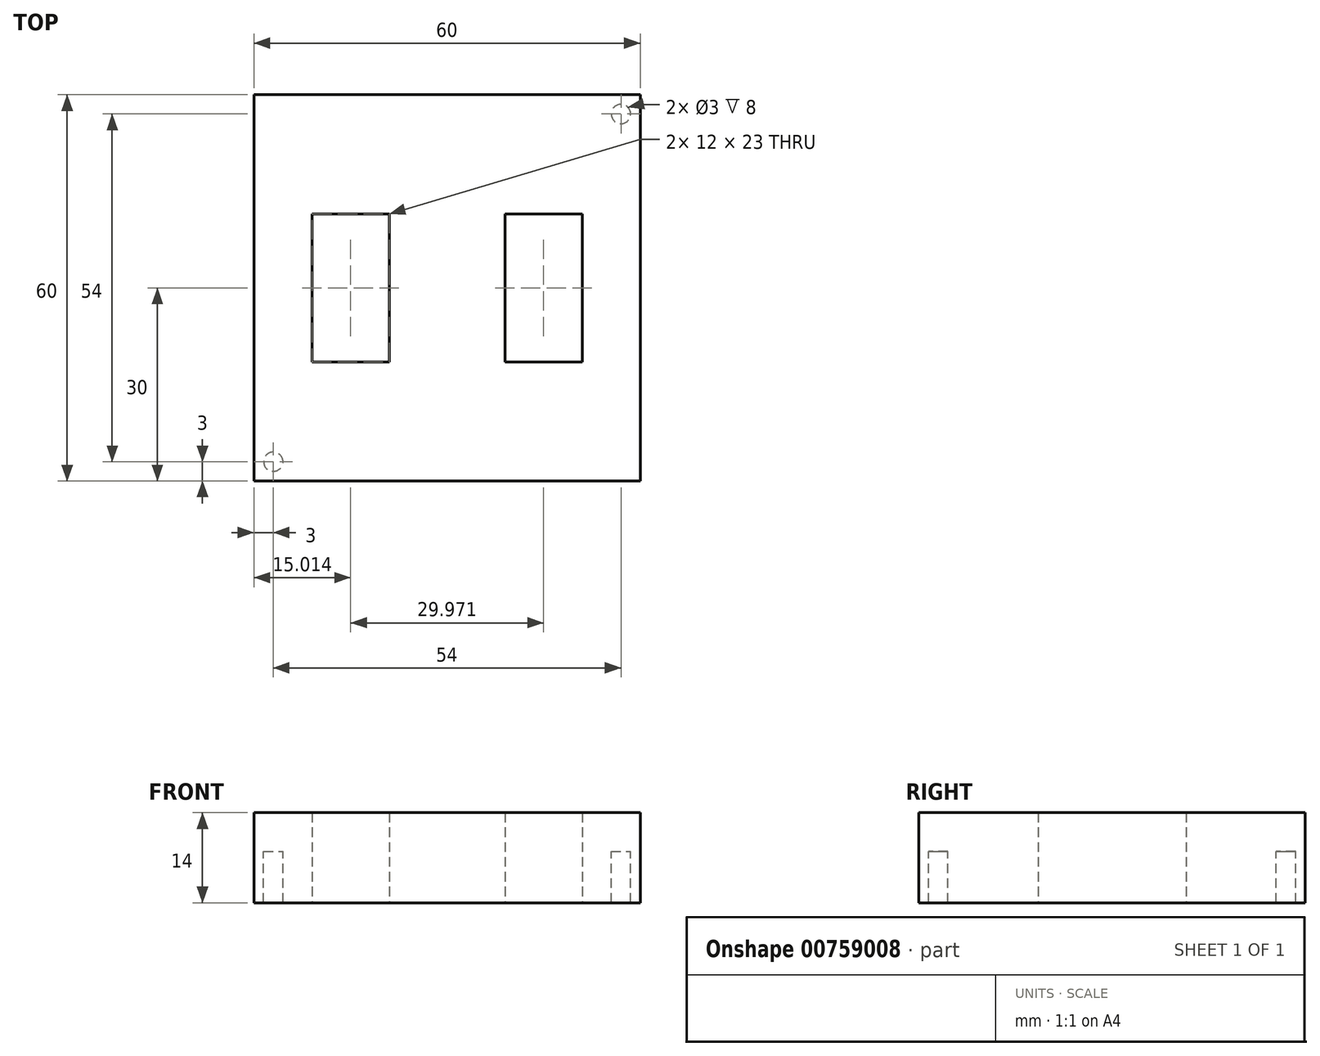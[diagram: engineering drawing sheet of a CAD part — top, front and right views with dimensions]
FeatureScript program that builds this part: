
annotation { "Feature Type Name" : "Feature", "Feature Type Description" : "" }
export const myFeature = defineFeature(function(context is Context, id is Id, definition is map)
    precondition{}
    {
        {
            var Q0;
            Q0=qCreatedBy(makeId("Top.planeOp"),FACE);
            var sketch = newSketch(context, id + "F0", { "sketchPlane" : qUnion([Q0])});
            skLineSegment(sketch, "E0.bottom", {"start": v(-30, 30) * mm, "end": v(30, 30) * mm});
            skLineSegment(sketch, "E0.top", {"start": v(-30, -30) * mm, "end": v(30, -30) * mm});
            skLineSegment(sketch, "E0.left", {"start": v(-30, 30) * mm, "end": v(-30, -30) * mm});
            skLineSegment(sketch, "E0.right", {"start": v(30, 30) * mm, "end": v(30, -30) * mm});
            skPoint(sketch, "E0.middle", {"position": v(0, 0) * mm});
            skLineSegment(sketch, "E1.bottom", {"start": v(8.99, 11.5) * mm, "end": v(20.99, 11.5) * mm});
            skLineSegment(sketch, "E1.top", {"start": v(8.99, -11.5) * mm, "end": v(20.99, -11.5) * mm});
            skLineSegment(sketch, "E1.left", {"start": v(8.99, 11.5) * mm, "end": v(8.99, -11.5) * mm});
            skLineSegment(sketch, "E1.right", {"start": v(20.99, 11.5) * mm, "end": v(20.99, -11.5) * mm});
            skPoint(sketch, "E1.middle", {"position": v(14.99, 0) * mm});
            skLineSegment(sketch, "E2.MirrorCS", {"start": v(-8.99, 11.5) * mm, "end": v(-20.99, 11.5) * mm});
            skLineSegment(sketch, "E3.MirrorCS", {"start": v(-8.99, 11.5) * mm, "end": v(-8.99, -11.5) * mm});
            skLineSegment(sketch, "E4.MirrorCS", {"start": v(-8.99, -11.5) * mm, "end": v(-20.99, -11.5) * mm});
            skLineSegment(sketch, "E5.MirrorCS", {"start": v(-20.99, 11.5) * mm, "end": v(-20.99, -11.5) * mm});
            skSolve(sketch);
        }
        {
            var Q0;
            Q0=makeQuery(id+"F0.imprint","IMPRINT",FACE,{"disambiguationData":[TD([[makeQuery(id+"F0.imprint","IMPRINT",EDGE,{"derivedFrom":sQuery(id+"F0.wireOp",EDGE,"E0.bottom")}),-1.0]])]});
            extrude(context, id + "F1", {"entities" : qUnion([Q0]), "depth" : 6 * mm, "offsetDistance" : 25 * mm});
        }
        {
            var Q0;
            Q0=makeQuery(id+"F1.opExtrude","CAP_FACE",FACE,{"disambiguationData":[OSD([sQuery(id+"F0.wireOp",EDGE,"E0.bottom"),sQuery(id+"F0.wireOp",EDGE,"E0.top"),sQuery(id+"F0.wireOp",EDGE,"E0.left"),sQuery(id+"F0.wireOp",EDGE,"E0.right"),sQuery(id+"F0.wireOp",EDGE,"HbzFISma-32Ek-z2c1-QKzy-2GvXbVWedbax.bottom"),sQuery(id+"F0.wireOp",EDGE,"HbzFISma-32Ek-z2c1-QKzy-2GvXbVWedbax.top"),sQuery(id+"F0.wireOp",EDGE,"HbzFISma-32Ek-z2c1-QKzy-2GvXbVWedbax.left"),sQuery(id+"F0.wireOp",EDGE,"HbzFISma-32Ek-z2c1-QKzy-2GvXbVWedbax.right")])],"isStart":true});
            var sketch = newSketch(context, id + "F2", { "sketchPlane" : qUnion([Q0])});
            skLineSegment(sketch, "E6", {"start": v(30, 30) * mm, "end": v(24, 30) * mm});
            skCircle(sketch, "E7", {"center": v(27, 27) * mm, "radius": 1.5 * mm});
            skCircle(sketch, "E8.MirrorC", {"center": v(27, -27) * mm, "radius": 1.5 * mm});
            skCircle(sketch, "E9.MirrorC", {"center": v(-27, 27) * mm, "radius": 1.5 * mm});
            skCircle(sketch, "E10.MirrorC", {"center": v(-27, -27) * mm, "radius": 1.5 * mm});
            skSolve(sketch);
        }
        {
            var Q0;
            Q0=makeQuery(id+"F2.imprint","IMPRINT",FACE,{"disambiguationData":[TD([[makeQuery(id+"F2.imprint","IMPRINT",EDGE,{"derivedFrom":sQuery(id+"F2.wireOp",EDGE,"E9.MirrorC")}),-1.0]])]});
            var Q1;
            Q1=makeQuery(id+"F2.imprint","IMPRINT",FACE,{"disambiguationData":[TD([[makeQuery(id+"F2.imprint","IMPRINT",EDGE,{"derivedFrom":sQuery(id+"F2.wireOp",EDGE,"E7")}),1.0]])]});
            var Q2;
            Q2=makeQuery(id+"F2.imprint","IMPRINT",FACE,{"disambiguationData":[TD([[makeQuery(id+"F2.imprint","IMPRINT",EDGE,{"derivedFrom":sQuery(id+"F2.wireOp",EDGE,"E8.MirrorC")}),-1.0]])]});
            var Q3;
            Q3=makeQuery(id+"F2.imprint","IMPRINT",FACE,{"disambiguationData":[TD([[makeQuery(id+"F2.imprint","IMPRINT",EDGE,{"derivedFrom":sQuery(id+"F2.wireOp",EDGE,"E10.MirrorC")}),1.0]])]});
            extrude(context, id + "F3", {"entities" : qUnion([Q0, Q1, Q2, Q3]), "operationType" : NewBodyOperationType.ADD, "depth" : 8 * mm, "offsetDistance" : 25 * mm});
        }
    });
